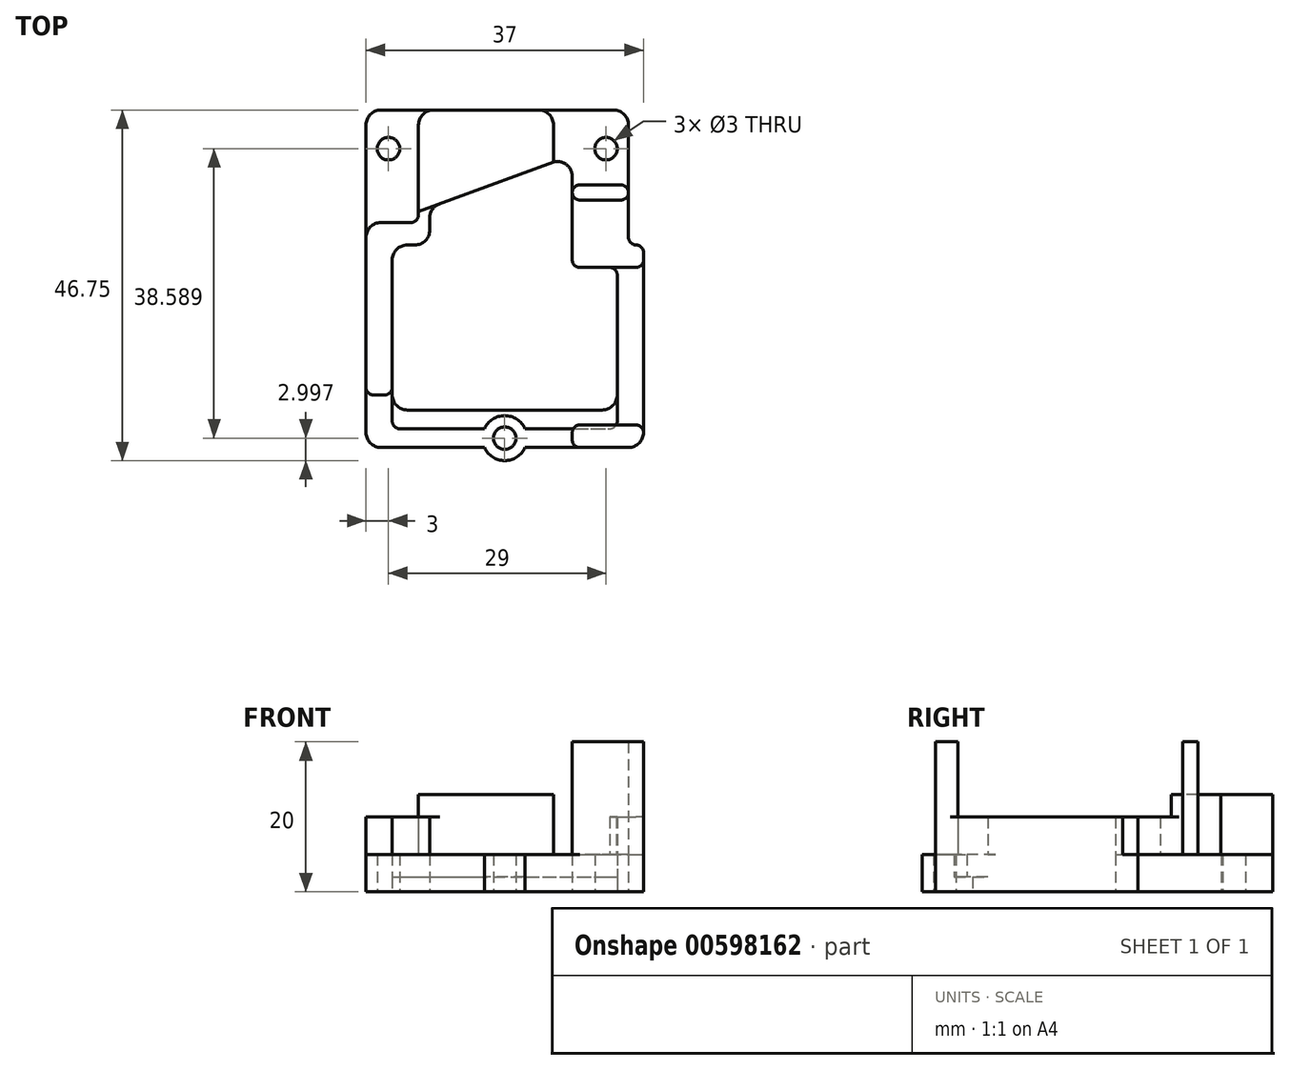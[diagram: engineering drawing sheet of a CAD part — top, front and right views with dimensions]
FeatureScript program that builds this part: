
annotation { "Feature Type Name" : "Feature", "Feature Type Description" : "" }
export const myFeature = defineFeature(function(context is Context, id is Id, definition is map)
    precondition{}
    {
        {
            var Q0;
            Q0=qCreatedBy(makeId("Top.planeOp"),FACE);
            var sketch = newSketch(context, id + "F0", { "sketchPlane" : qUnion([Q0])});
            skLineSegment(sketch, "E0.bottom", {"start": v(14.5, 22.5) * mm, "end": v(-16.5, 22.5) * mm});
            skLineSegment(sketch, "E0.top", {"start": v(16.5, -22.5) * mm, "end": v(-16.5, -22.5) * mm});
            skLineSegment(sketch, "E0.left", {"start": v(18.5, 3.5) * mm, "end": v(18.5, -20.5) * mm});
            skLineSegment(sketch, "E0.right", {"start": v(-18.5, 20.5) * mm, "end": v(-18.5, -20.5) * mm});
            skPoint(sketch, "E0.middle", {"position": v(0, 0) * mm});
            skLineSegment(sketch, "E1", {"start": v(-15, 2.5) * mm, "end": v(-15, -15.5) * mm});
            skLineSegment(sketch, "E2", {"start": v(-13, -17.5) * mm, "end": v(13, -17.5) * mm});
            skLineSegment(sketch, "E3", {"start": v(15, -15.5) * mm, "end": v(15, 0.5) * mm});
            skLineSegment(sketch, "E4", {"start": v(-13, 4.5) * mm, "end": v(-12, 4.5) * mm});
            skLineSegment(sketch, "E5", {"start": v(-10, 6.5) * mm, "end": v(-10, 8.1) * mm});
            skLineSegment(sketch, "E6", {"start": v(-8.7, 9.98) * mm, "end": v(6.3, 15.5) * mm});
            skLineSegment(sketch, "E7", {"start": v(9, 13.63) * mm, "end": v(9, 2.5) * mm});
            skLineSegment(sketch, "E8", {"start": v(10, 1.5) * mm, "end": v(14, 1.5) * mm});
            skLineSegment(sketch, "E9", {"start": v(16.5, 20.5) * mm, "end": v(16.5, 5.5) * mm});
            skLineSegment(sketch, "E10", {"start": v(17.5, 4.5) * mm, "end": v(17.5, 4.5) * mm});
            skPoint(sketch, "E11.visualSharp", {"position": v(-15, -17.5) * mm});
            skArc(sketch, "E11.filletArc", {"start": v(-15, -15.5) * mm, "mid": v(-14.41, -16.91) * mm, "end": v(-13, -17.5) * mm});
            skPoint(sketch, "E12.visualSharp", {"position": v(-15, 4.5) * mm});
            skArc(sketch, "E12.filletArc", {"start": v(-13, 4.5) * mm, "mid": v(-14.41, 3.91) * mm, "end": v(-15, 2.5) * mm});
            skPoint(sketch, "E13.visualSharp", {"position": v(-10, 4.5) * mm});
            skArc(sketch, "E13.filletArc", {"start": v(-12, 4.5) * mm, "mid": v(-10.59, 5.09) * mm, "end": v(-10, 6.5) * mm});
            skPoint(sketch, "E14.visualSharp", {"position": v(-10, 9.5) * mm});
            skArc(sketch, "E14.filletArc", {"start": v(-8.7, 9.98) * mm, "mid": v(-9.64, 9.25) * mm, "end": v(-10, 8.1) * mm});
            skPoint(sketch, "E15.visualSharp", {"position": v(9, 16.5) * mm});
            skArc(sketch, "E15.filletArc", {"start": v(9, 13.63) * mm, "mid": v(8.14, 15.27) * mm, "end": v(6.3, 15.5) * mm});
            skPoint(sketch, "E16.visualSharp", {"position": v(-18.5, 22.5) * mm});
            skArc(sketch, "E16.filletArc", {"start": v(-16.5, 22.5) * mm, "mid": v(-17.91, 21.91) * mm, "end": v(-18.5, 20.5) * mm});
            skPoint(sketch, "E17.orphan", {"position": v(18.5, 22.5) * mm});
            skPoint(sketch, "E18.visualSharp", {"position": v(16.5, 22.5) * mm});
            skArc(sketch, "E18.filletArc", {"start": v(16.5, 20.5) * mm, "mid": v(15.91, 21.91) * mm, "end": v(14.5, 22.5) * mm});
            skPoint(sketch, "E19.visualSharp", {"position": v(18.5, -22.5) * mm});
            skArc(sketch, "E19.filletArc", {"start": v(16.5, -22.5) * mm, "mid": v(17.91, -21.91) * mm, "end": v(18.5, -20.5) * mm});
            skPoint(sketch, "E20.visualSharp", {"position": v(-18.5, -22.5) * mm});
            skArc(sketch, "E20.filletArc", {"start": v(-18.5, -20.5) * mm, "mid": v(-17.91, -21.91) * mm, "end": v(-16.5, -22.5) * mm});
            skPoint(sketch, "E21.visualSharp", {"position": v(15, -17.5) * mm});
            skArc(sketch, "E21.filletArc", {"start": v(13, -17.5) * mm, "mid": v(14.41, -16.91) * mm, "end": v(15, -15.5) * mm});
            skPoint(sketch, "E22.visualSharp", {"position": v(16.5, 4.5) * mm});
            skArc(sketch, "E22.filletArc", {"start": v(16.5, 5.5) * mm, "mid": v(16.8, 4.8) * mm, "end": v(17.5, 4.5) * mm});
            skPoint(sketch, "E23.visualSharp", {"position": v(9, 1.5) * mm});
            skArc(sketch, "E23.filletArc", {"start": v(9, 2.5) * mm, "mid": v(9.3, 1.8) * mm, "end": v(10, 1.5) * mm});
            skPoint(sketch, "E24.visualSharp", {"position": v(15, 1.5) * mm});
            skArc(sketch, "E24.filletArc", {"start": v(15, 0.5) * mm, "mid": v(14.7, 1.2) * mm, "end": v(14, 1.5) * mm});
            skPoint(sketch, "E25.visualSharp", {"position": v(18.5, 4.5) * mm});
            skArc(sketch, "E25.filletArc", {"start": v(18.5, 3.5) * mm, "mid": v(18.2, 4.2) * mm, "end": v(17.5, 4.5) * mm});
            skLineSegment(sketch, "E26", {"start": v(-14, -20) * mm, "end": v(14, -20) * mm});
            skLineSegment(sketch, "E27", {"start": v(-15, -15.5) * mm, "end": v(-15, -19) * mm});
            skLineSegment(sketch, "E28", {"start": v(15, -15.5) * mm, "end": v(15, -19) * mm});
            skPoint(sketch, "E29.visualSharp", {"position": v(-15, -20) * mm});
            skArc(sketch, "E29.filletArc", {"start": v(-15, -19) * mm, "mid": v(-14.7, -19.7) * mm, "end": v(-14, -20) * mm});
            skPoint(sketch, "E30.visualSharp", {"position": v(15, -20) * mm});
            skArc(sketch, "E30.filletArc", {"start": v(14, -20) * mm, "mid": v(14.7, -19.7) * mm, "end": v(15, -19) * mm});
            skLineSegment(sketch, "E31", {"start": v(0, -17.5) * mm, "end": v(0, -23.5) * mm, "construction": true});
            skPoint(sketch, "E31.endSnap0", {"position": v(0, -17.5) * mm});
            skCircle(sketch, "E32", {"center": v(0, -21.25) * mm, "radius": 3 * mm});
            skCircle(sketch, "E33", {"center": v(0, -21.25) * mm, "radius": 1.5 * mm});
            skCircle(sketch, "E34", {"center": v(-15.5, 17.34) * mm, "radius": 3 * mm});
            skCircle(sketch, "E35", {"center": v(-15.5, 17.34) * mm, "radius": 1.5 * mm});
            skLineSegment(sketch, "E36", {"start": v(-15.5, 17.34) * mm, "end": v(15.54, 17.34) * mm, "construction": true});
            skCircle(sketch, "E37", {"center": v(13.5, 17.34) * mm, "radius": 3 * mm});
            skCircle(sketch, "E38", {"center": v(13.5, 17.34) * mm, "radius": 1.5 * mm});
            skSolve(sketch);
        }
        {
            var Q0;
            Q0=makeQuery(id+"F0.imprint","IMPRINT",FACE,{"disambiguationData":[TD([[makeQuery(id+"F0.imprint","IMPRINT",EDGE,{"derivedFrom":sQuery(id+"F0.wireOp",EDGE,"E2")}),-1.0]])]});
            extrude(context, id + "F1", {"entities" : qUnion([Q0]), "depth" : 2 * mm, "offsetDistance" : 25 * mm});
        }
        {
            var Q0;
            Q0=makeQuery(id+"F0.imprint","IMPRINT",FACE,{"disambiguationData":[TD([[makeQuery(id+"F0.imprint","IMPRINT",EDGE,{"derivedFrom":sQuery(id+"F0.wireOp",EDGE,"E0.bottom")}),1.0]])]});
            var Q1;
            {var subQ0=sQuery(id+"F0.wireOp",EDGE,"E32");var subQ1=sQuery(id+"F0.wireOp",EDGE,"E0.top");var subQ2=makeQuery(id+"F0.imprint","INTERSECT",VERTEX,{"disambiguationData":[OD(1.0)],"derivedFrom":[subQ1,subQ0]});Q1=makeQuery(id+"F0.imprint","IMPRINT",FACE,{"disambiguationData":[TD([[makeQuery(id+"F0.imprint","IMPRINT",EDGE,{"disambiguationData":[TD([[subQ2,1.0]])],"derivedFrom":subQ1}),-1.0]])]});}
            var Q2;
            {var subQ0=sQuery(id+"F0.wireOp",EDGE,"E32");var subQ1=sQuery(id+"F0.wireOp",EDGE,"E0.top");var subQ2=makeQuery(id+"F0.imprint","INTERSECT",VERTEX,{"disambiguationData":[OD(0.0)],"derivedFrom":[subQ1,subQ0]});Q2=makeQuery(id+"F0.imprint","IMPRINT",FACE,{"disambiguationData":[TD([[makeQuery(id+"F0.imprint","IMPRINT",EDGE,{"disambiguationData":[TD([[subQ2,-1.0]])],"derivedFrom":subQ1}),1.0]])]});}
            var Q3;
            {var subQ0=sQuery(id+"F0.wireOp",EDGE,"E32");var subQ1=sQuery(id+"F0.wireOp",EDGE,"E0.top");var subQ2=makeQuery(id+"F0.imprint","INTERSECT",VERTEX,{"disambiguationData":[OD(0.0)],"derivedFrom":[subQ1,subQ0]});Q3=makeQuery(id+"F0.imprint","IMPRINT",FACE,{"disambiguationData":[TD([[makeQuery(id+"F0.imprint","IMPRINT",EDGE,{"disambiguationData":[TD([[subQ2,-1.0]])],"derivedFrom":subQ1}),-1.0]])]});}
            var Q4;
            {var subQ0=sQuery(id+"F0.wireOp",EDGE,"E32");var subQ1=sQuery(id+"F0.wireOp",EDGE,"E26");var subQ2=makeQuery(id+"F0.imprint","INTERSECT",VERTEX,{"disambiguationData":[OD(0.0)],"derivedFrom":[subQ1,subQ0]});Q4=makeQuery(id+"F0.imprint","IMPRINT",FACE,{"disambiguationData":[TD([[makeQuery(id+"F0.imprint","IMPRINT",EDGE,{"disambiguationData":[TD([[subQ2,-1.0]])],"derivedFrom":subQ1}),1.0]])]});}
            var Q5;
            Q5=makeQuery(id+"F0.imprint","IMPRINT",FACE,{"disambiguationData":[TD([[makeQuery(id+"F0.imprint","IMPRINT",EDGE,{"derivedFrom":sQuery(id+"F0.wireOp",EDGE,"E34")}),1.0]])]});
            var Q6;
            Q6=makeQuery(id+"F0.imprint","IMPRINT",FACE,{"disambiguationData":[TD([[makeQuery(id+"F0.imprint","IMPRINT",EDGE,{"derivedFrom":sQuery(id+"F0.wireOp",EDGE,"E37")}),1.0]])]});
            extrude(context, id + "F2", {"entities" : qUnion([Q0, Q1, Q2, Q3, Q4, Q5, Q6]), "operationType" : NewBodyOperationType.ADD, "depth" : 5 * mm, "offsetDistance" : 25 * mm});
        }
        {
            var Q0;
            Q0=makeQuery(id+"F2.opExtrude","CAP_FACE",FACE,{"disambiguationData":[OSD([sQuery(id+"F0.wireOp",EDGE,"E0.bottom"),sQuery(id+"F0.wireOp",EDGE,"E0.top"),sQuery(id+"F0.wireOp",EDGE,"E0.left"),sQuery(id+"F0.wireOp",EDGE,"E0.right"),sQuery(id+"F0.wireOp",EDGE,"E1"),sQuery(id+"F0.wireOp",EDGE,"E3"),sQuery(id+"F0.wireOp",EDGE,"E4"),sQuery(id+"F0.wireOp",EDGE,"E5"),sQuery(id+"F0.wireOp",EDGE,"E6"),sQuery(id+"F0.wireOp",EDGE,"E7"),sQuery(id+"F0.wireOp",EDGE,"E8"),sQuery(id+"F0.wireOp",EDGE,"E9"),sQuery(id+"F0.wireOp",EDGE,"E12.filletArc"),sQuery(id+"F0.wireOp",EDGE,"E13.filletArc"),sQuery(id+"F0.wireOp",EDGE,"E14.filletArc"),sQuery(id+"F0.wireOp",EDGE,"E15.filletArc"),sQuery(id+"F0.wireOp",EDGE,"E16.filletArc"),sQuery(id+"F0.wireOp",EDGE,"E18.filletArc"),sQuery(id+"F0.wireOp",EDGE,"E19.filletArc"),sQuery(id+"F0.wireOp",EDGE,"E20.filletArc"),sQuery(id+"F0.wireOp",EDGE,"E22.filletArc"),sQuery(id+"F0.wireOp",EDGE,"E23.filletArc"),sQuery(id+"F0.wireOp",EDGE,"E24.filletArc"),sQuery(id+"F0.wireOp",EDGE,"E25.filletArc"),sQuery(id+"F0.wireOp",EDGE,"E26"),sQuery(id+"F0.wireOp",EDGE,"E27"),sQuery(id+"F0.wireOp",EDGE,"E28"),sQuery(id+"F0.wireOp",EDGE,"E29.filletArc"),sQuery(id+"F0.wireOp",EDGE,"E30.filletArc"),sQuery(id+"F0.wireOp",EDGE,"E32"),sQuery(id+"F0.wireOp",EDGE,"E33"),sQuery(id+"F0.wireOp",EDGE,"E35"),sQuery(id+"F0.wireOp",EDGE,"E38")])],"isStart":false});
            var sketch = newSketch(context, id + "F3", { "sketchPlane" : qUnion([Q0])});
            skLineSegment(sketch, "E39", {"start": v(-17.5, -15.5) * mm, "end": v(-16, -15.5) * mm});
            skLineSegment(sketch, "E40", {"start": v(-12.5, 7.5) * mm, "end": v(-16.5, 7.5) * mm});
            skLineSegment(sketch, "E41", {"start": v(-11.5, 8.5) * mm, "end": v(-11.5, 20.5) * mm});
            skLineSegment(sketch, "E42", {"start": v(6.5, 20.5) * mm, "end": v(6.5, 15.58) * mm});
            skLineSegment(sketch, "E43", {"start": v(-9.5, 22.5) * mm, "end": v(4.5, 22.5) * mm});
            skLineSegment(sketch, "E44", {"start": v(6.5, 15.58) * mm, "end": v(-8.7, 9.98) * mm});
            skLineSegment(sketch, "E45", {"start": v(-8.7, 9.98) * mm, "end": v(-11.5, 8.95) * mm});
            skLineSegment(sketch, "E46", {"start": v(-18.5, -14.5) * mm, "end": v(-18.5, 5.5) * mm});
            skLineSegment(sketch, "E47", {"start": v(-15, -14.5) * mm, "end": v(-15, 2.5) * mm});
            skPoint(sketch, "E48.visualSharp", {"position": v(-11.5, 22.5) * mm});
            skArc(sketch, "E48.filletArc", {"start": v(-9.5, 22.5) * mm, "mid": v(-10.91, 21.91) * mm, "end": v(-11.5, 20.5) * mm});
            skPoint(sketch, "E49.visualSharp", {"position": v(6.5, 22.5) * mm});
            skArc(sketch, "E49.filletArc", {"start": v(6.5, 20.5) * mm, "mid": v(5.91, 21.91) * mm, "end": v(4.5, 22.5) * mm});
            skPoint(sketch, "E50.visualSharp", {"position": v(-18.5, 7.5) * mm});
            skArc(sketch, "E50.filletArc", {"start": v(-16.5, 7.5) * mm, "mid": v(-17.91, 6.91) * mm, "end": v(-18.5, 5.5) * mm});
            skPoint(sketch, "E51.visualSharp", {"position": v(-18.5, -15.5) * mm});
            skArc(sketch, "E51.filletArc", {"start": v(-18.5, -14.5) * mm, "mid": v(-18.2, -15.2) * mm, "end": v(-17.5, -15.5) * mm});
            skPoint(sketch, "E52.visualSharp", {"position": v(-15, -15.5) * mm});
            skArc(sketch, "E52.filletArc", {"start": v(-16, -15.5) * mm, "mid": v(-15.3, -15.2) * mm, "end": v(-15, -14.5) * mm});
            skPoint(sketch, "E53.visualSharp", {"position": v(-11.5, 7.5) * mm});
            skArc(sketch, "E53.filletArc", {"start": v(-12.5, 7.5) * mm, "mid": v(-11.8, 7.8) * mm, "end": v(-11.5, 8.5) * mm});
            skLineSegment(sketch, "E54.bottom", {"start": v(10, 12.5) * mm, "end": v(15.5, 12.5) * mm});
            skLineSegment(sketch, "E54.top", {"start": v(10, 10.5) * mm, "end": v(15.5, 10.5) * mm});
            skLineSegment(sketch, "E54.left", {"start": v(9, 11.5) * mm, "end": v(9, 11.5) * mm});
            skLineSegment(sketch, "E54.right", {"start": v(16.5, 11.5) * mm, "end": v(16.5, 11.5) * mm});
            skLineSegment(sketch, "E55.bottom", {"start": v(9, 1.5) * mm, "end": v(17.5, 1.5) * mm});
            skLineSegment(sketch, "E55.top", {"start": v(10, 4.5) * mm, "end": v(18.5, 4.5) * mm});
            skLineSegment(sketch, "E55.left", {"start": v(9, 1.5) * mm, "end": v(9, 3.5) * mm});
            skLineSegment(sketch, "E55.right", {"start": v(18.5, 2.5) * mm, "end": v(18.5, 4.5) * mm});
            skLineSegment(sketch, "E56.bottom", {"start": v(10, -22.5) * mm, "end": v(18.5, -22.5) * mm});
            skLineSegment(sketch, "E56.top", {"start": v(10, -19.5) * mm, "end": v(17.5, -19.5) * mm});
            skLineSegment(sketch, "E56.left", {"start": v(9, -21.5) * mm, "end": v(9, -20.5) * mm});
            skLineSegment(sketch, "E56.right", {"start": v(18.5, -22.5) * mm, "end": v(18.5, -20.5) * mm});
            skLineSegment(sketch, "E57.bottom", {"start": v(12.25, 4.5) * mm, "end": v(13.25, 4.5) * mm});
            skLineSegment(sketch, "E57.left", {"start": v(12.25, 4.5) * mm, "end": v(12.25, 10.5) * mm});
            skLineSegment(sketch, "E57.right", {"start": v(13.25, 4.5) * mm, "end": v(13.25, 10.5) * mm});
            skPoint(sketch, "E57.middle", {"position": v(12.75, 10.5) * mm});
            skPoint(sketch, "E58.trimOffspring.end.orphan", {"position": v(13.25, 16.5) * mm});
            skPoint(sketch, "E59.trimOffspring.end.orphan", {"position": v(12.25, 16.5) * mm});
            skPoint(sketch, "E60.visualSharp", {"position": v(9, 4.5) * mm});
            skArc(sketch, "E60.filletArc", {"start": v(10, 4.5) * mm, "mid": v(9.3, 4.2) * mm, "end": v(9, 3.5) * mm});
            skPoint(sketch, "E61.visualSharp", {"position": v(18.5, 1.5) * mm});
            skArc(sketch, "E61.filletArc", {"start": v(17.5, 1.5) * mm, "mid": v(18.2, 1.8) * mm, "end": v(18.5, 2.5) * mm});
            skPoint(sketch, "E62.visualSharp", {"position": v(9, 10.5) * mm});
            skArc(sketch, "E62.filletArc", {"start": v(9, 11.5) * mm, "mid": v(9.3, 10.8) * mm, "end": v(10, 10.5) * mm});
            skPoint(sketch, "E63.visualSharp", {"position": v(9, 12.5) * mm});
            skArc(sketch, "E63.filletArc", {"start": v(10, 12.5) * mm, "mid": v(9.3, 12.2) * mm, "end": v(9, 11.5) * mm});
            skPoint(sketch, "E64.visualSharp", {"position": v(16.5, 12.5) * mm});
            skArc(sketch, "E64.filletArc", {"start": v(16.5, 11.5) * mm, "mid": v(16.2, 12.2) * mm, "end": v(15.5, 12.5) * mm});
            skPoint(sketch, "E65.visualSharp", {"position": v(16.5, 10.5) * mm});
            skArc(sketch, "E65.filletArc", {"start": v(15.5, 10.5) * mm, "mid": v(16.2, 10.8) * mm, "end": v(16.5, 11.5) * mm});
            skPoint(sketch, "E66.visualSharp", {"position": v(9, -19.5) * mm});
            skArc(sketch, "E66.filletArc", {"start": v(10, -19.5) * mm, "mid": v(9.3, -19.8) * mm, "end": v(9, -20.5) * mm});
            skPoint(sketch, "E67.visualSharp", {"position": v(9, -22.5) * mm});
            skArc(sketch, "E67.filletArc", {"start": v(9, -21.5) * mm, "mid": v(9.3, -22.2) * mm, "end": v(10, -22.5) * mm});
            skPoint(sketch, "E68.visualSharp", {"position": v(18.5, -19.5) * mm});
            skArc(sketch, "E68.filletArc", {"start": v(18.5, -20.5) * mm, "mid": v(18.2, -19.8) * mm, "end": v(17.5, -19.5) * mm});
            skSolve(sketch);
        }
        {
            var Q0;
            Q0=makeQuery(id+"F3.imprint","IMPRINT",FACE,{"disambiguationData":[TD([[makeQuery(id+"F3.imprint","IMPRINT",EDGE,{"derivedFrom":sQuery(id+"F3.wireOp",EDGE,"E39")}),1.0]])]});
            extrude(context, id + "F4", {"entities" : qUnion([Q0]), "operationType" : NewBodyOperationType.ADD, "depth" : 5 * mm, "offsetDistance" : 25 * mm});
        }
        {
            var Q0;
            {var subQ2=sQuery(id+"F3.wireOp",EDGE,"E42");Q0=makeQuery(id+"F3.imprint","IMPRINT",FACE,{"disambiguationData":[TD([[makeQuery(id+"F3.imprint","IMPRINT",EDGE,{"derivedFrom":subQ2}),-1.0]])]});}
            extrude(context, id + "F5", {"entities" : qUnion([Q0]), "operationType" : NewBodyOperationType.ADD, "depth" : 8 * mm, "offsetDistance" : 25 * mm});
        }
        {
            var Q0;
            {var subQ1=sQuery(id+"F3.wireOp",EDGE,"E56.left");Q0=makeQuery(id+"F3.imprint","IMPRINT",FACE,{"disambiguationData":[TD([[makeQuery(id+"F3.imprint","IMPRINT",EDGE,{"derivedFrom":subQ1}),-1.0]])]});}
            var Q1;
            {var subQ0=sQuery(id+"F3.wireOp",EDGE,"E66.filletArc");var subQ1=sQuery(id+"F3.wireOp",EDGE,"E56.top");var subQ2=makeQuery(id+"F3.imprint","INTERSECT",VERTEX,{"derivedFrom":[subQ1,subQ0]});Q1=makeQuery(id+"F3.imprint","IMPRINT",FACE,{"disambiguationData":[TD([[makeQuery(id+"F3.imprint","IMPRINT",EDGE,{"disambiguationData":[TD([[subQ2,-1.0]])],"derivedFrom":subQ1}),-1.0]])]});}
            extrude(context, id + "F6", {"entities" : qUnion([Q0, Q1]), "operationType" : NewBodyOperationType.ADD, "depth" : 15 * mm, "offsetDistance" : 25 * mm});
        }
        {
            var Q0;
            Q0=makeQuery(id+"F3.imprint","IMPRINT",FACE,{"disambiguationData":[TD([[makeQuery(id+"F3.imprint","IMPRINT",EDGE,{"derivedFrom":sQuery(id+"F3.wireOp",EDGE,"E54.bottom")}),-1.0]])]});
            var Q1;
            {var subQ1=sQuery(id+"F3.wireOp",EDGE,"E57.bottom");Q1=makeQuery(id+"F3.imprint","IMPRINT",FACE,{"disambiguationData":[TD([[makeQuery(id+"F3.imprint","IMPRINT",EDGE,{"derivedFrom":subQ1}),-1.0]])]});}
            extrude(context, id + "F7", {"entities" : qUnion([Q0, Q1]), "operationType" : NewBodyOperationType.ADD, "depth" : 15 * mm, "offsetDistance" : 25 * mm});
        }
        {
            var Q0;
            Q0=makeQuery(id+"F3.imprint","IMPRINT",FACE,{"disambiguationData":[TD([[makeQuery(id+"F3.imprint","IMPRINT",EDGE,{"derivedFrom":sQuery(id+"F3.wireOp",EDGE,"E57.bottom")}),1.0]])]});
            var Q1;
            {var subQ0=sQuery(id+"F3.wireOp",EDGE,"E61.filletArc");Q1=makeQuery(id+"F3.imprint","IMPRINT",FACE,{"disambiguationData":[TD([[makeQuery(id+"F3.imprint","IMPRINT",EDGE,{"derivedFrom":subQ0}),-1.0]])]});}
            extrude(context, id + "F8", {"entities" : qUnion([Q0, Q1]), "operationType" : NewBodyOperationType.ADD, "depth" : 5 * mm, "offsetDistance" : 25 * mm});
        }
    });
